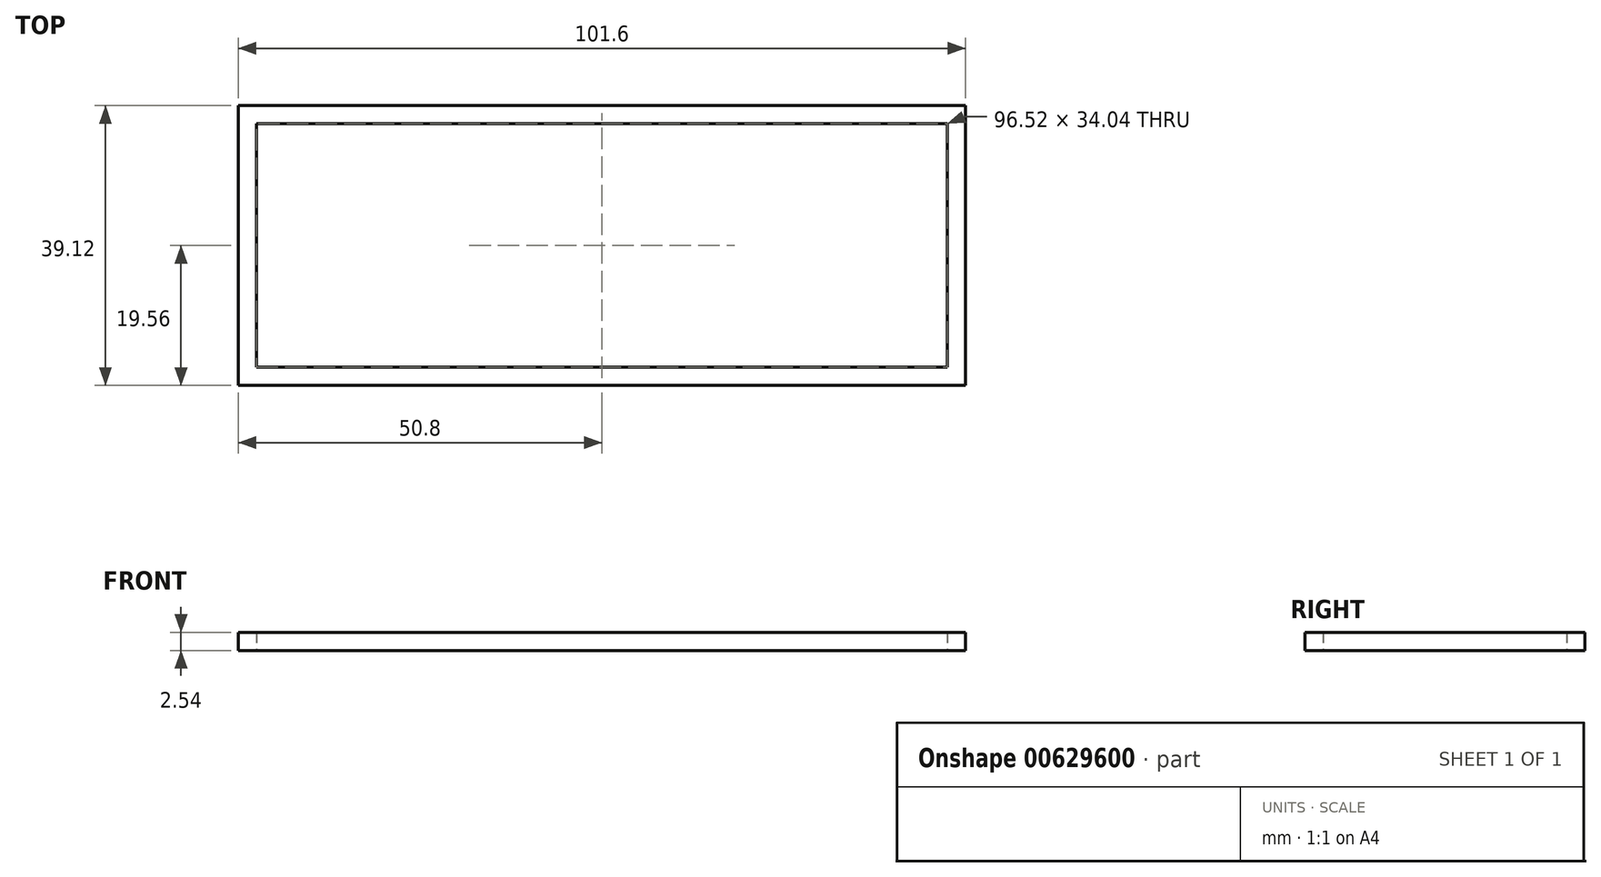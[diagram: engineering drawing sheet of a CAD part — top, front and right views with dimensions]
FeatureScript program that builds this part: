
annotation { "Feature Type Name" : "Feature", "Feature Type Description" : "" }
export const myFeature = defineFeature(function(context is Context, id is Id, definition is map)
    precondition{}
    {
        {
            var Q0;
            Q0=qCreatedBy(makeId("Top.planeOp"),FACE);
            var sketch = newSketch(context, id + "F0", { "sketchPlane" : qUnion([Q0])});
            skLineSegment(sketch, "E0.bottom", {"start": v(-48.26, 17.02) * mm, "end": v(48.26, 17.02) * mm});
            skLineSegment(sketch, "E0.top", {"start": v(-48.26, -17.02) * mm, "end": v(48.26, -17.02) * mm});
            skLineSegment(sketch, "E0.left", {"start": v(-48.26, 17.02) * mm, "end": v(-48.26, -17.02) * mm});
            skLineSegment(sketch, "E0.right", {"start": v(48.26, 17.02) * mm, "end": v(48.26, -17.02) * mm});
            skPoint(sketch, "E0.middle", {"position": v(0, 0) * mm});
            skLineSegment(sketch, "E1.bottom", {"start": v(-50.8, 19.56) * mm, "end": v(50.8, 19.56) * mm});
            skLineSegment(sketch, "E1.top", {"start": v(-50.8, -19.56) * mm, "end": v(50.8, -19.56) * mm});
            skLineSegment(sketch, "E1.left", {"start": v(-50.8, 19.56) * mm, "end": v(-50.8, -19.56) * mm});
            skLineSegment(sketch, "E1.right", {"start": v(50.8, 19.56) * mm, "end": v(50.8, -19.56) * mm});
            skLineSegment(sketch, "E2", {"start": v(-48.26, 17.02) * mm, "end": v(-48.26, 19.56) * mm, "construction": true});
            skLineSegment(sketch, "E3", {"start": v(-48.26, 17.02) * mm, "end": v(-50.8, 17.02) * mm, "construction": true});
            skSolve(sketch);
        }
        {
            var Q0;
            Q0 = qSketchRegion(id + "F0", true);
            extrude(context, id + "F1", {"entities" : qUnion([Q0]), "depth" : 2.54 * mm, "offsetDistance" : 25.4 * mm});
        }
    });
